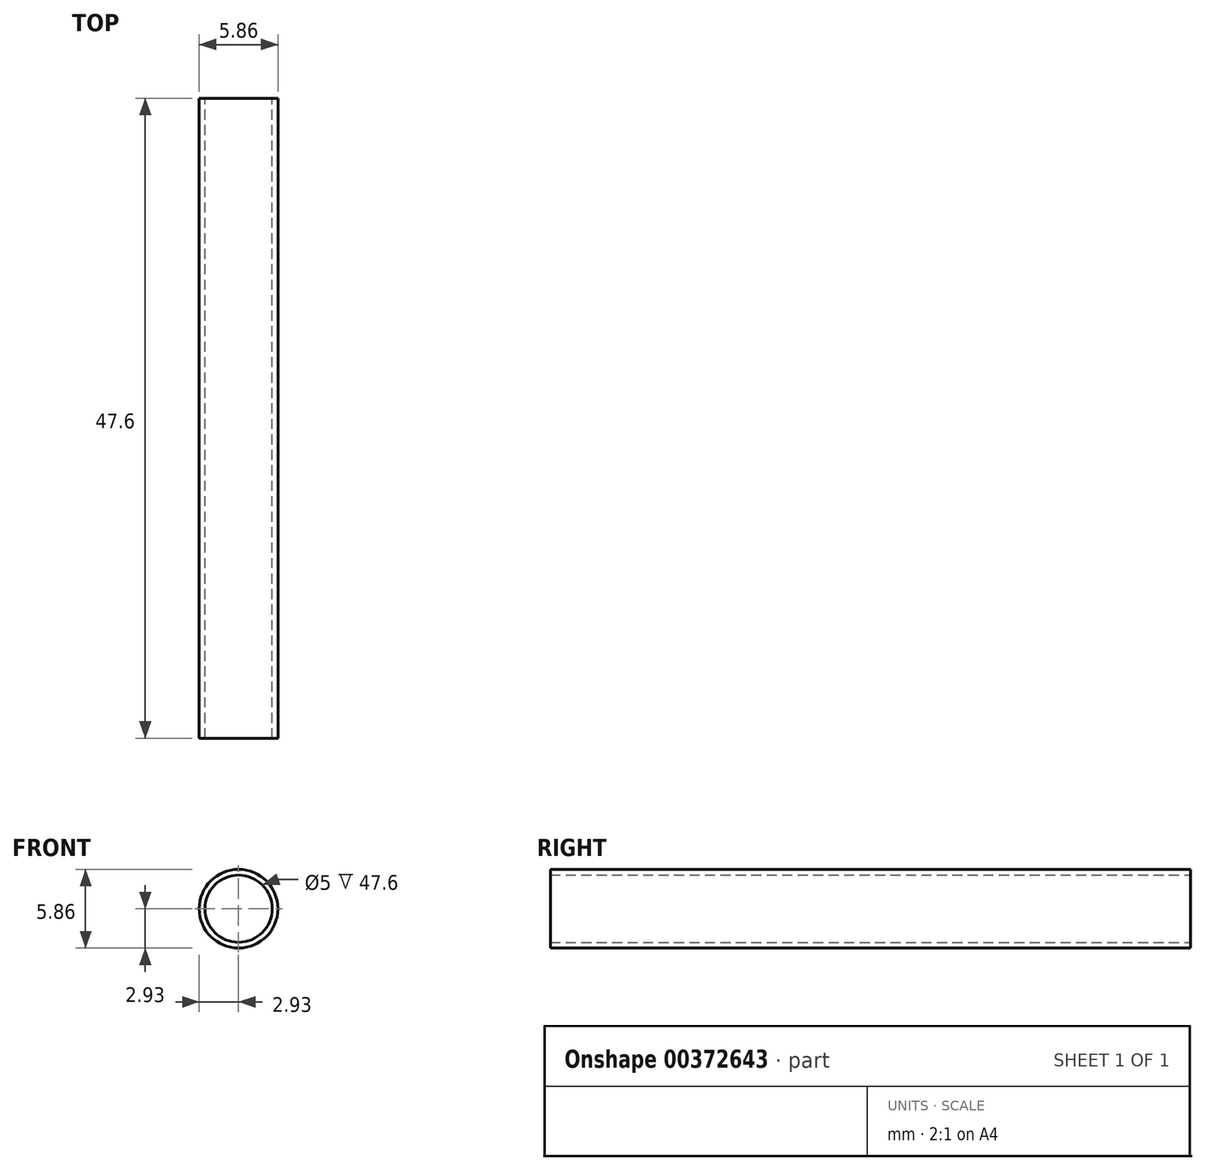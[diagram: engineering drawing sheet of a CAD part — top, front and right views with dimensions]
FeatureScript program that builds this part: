
annotation { "Feature Type Name" : "Feature", "Feature Type Description" : "" }
export const myFeature = defineFeature(function(context is Context, id is Id, definition is map)
    precondition{}
    {
        {
            var Q0;
            Q0=qCreatedBy(makeId("Front.planeOp"), FACE);
            var sketch = newSketch(context, id + "F0", { "sketchPlane" : qUnion([Q0]), "disableImprinting" : false});
            skCircle(sketch, "E0", {"center": v(0, 0) * mm, "radius": 2.93 * mm});
            skCircle(sketch, "E1", {"center": v(0, 0) * mm, "radius": 2.5 * mm});
            skSolve(sketch);
        }
        {
            var Q0;
            Q0 = qSketchRegion(id + "F0", true);
            extrude(context, id + "F1", {"entities" : qUnion([Q0]), "flatOperationType" : FlatOperationType.REMOVE, "thickness1" : 5 * mm, "thickness2" : 0 * mm, "thickness" : 5 * mm, "depth" : 47.6 * mm, "offsetDistance" : 25 * mm, "startOffsetBound" : StartOffsetType.BLIND, "startOffsetDistance" : 25 * mm, "domain" : OperationDomain.MODEL});
        }
    });
